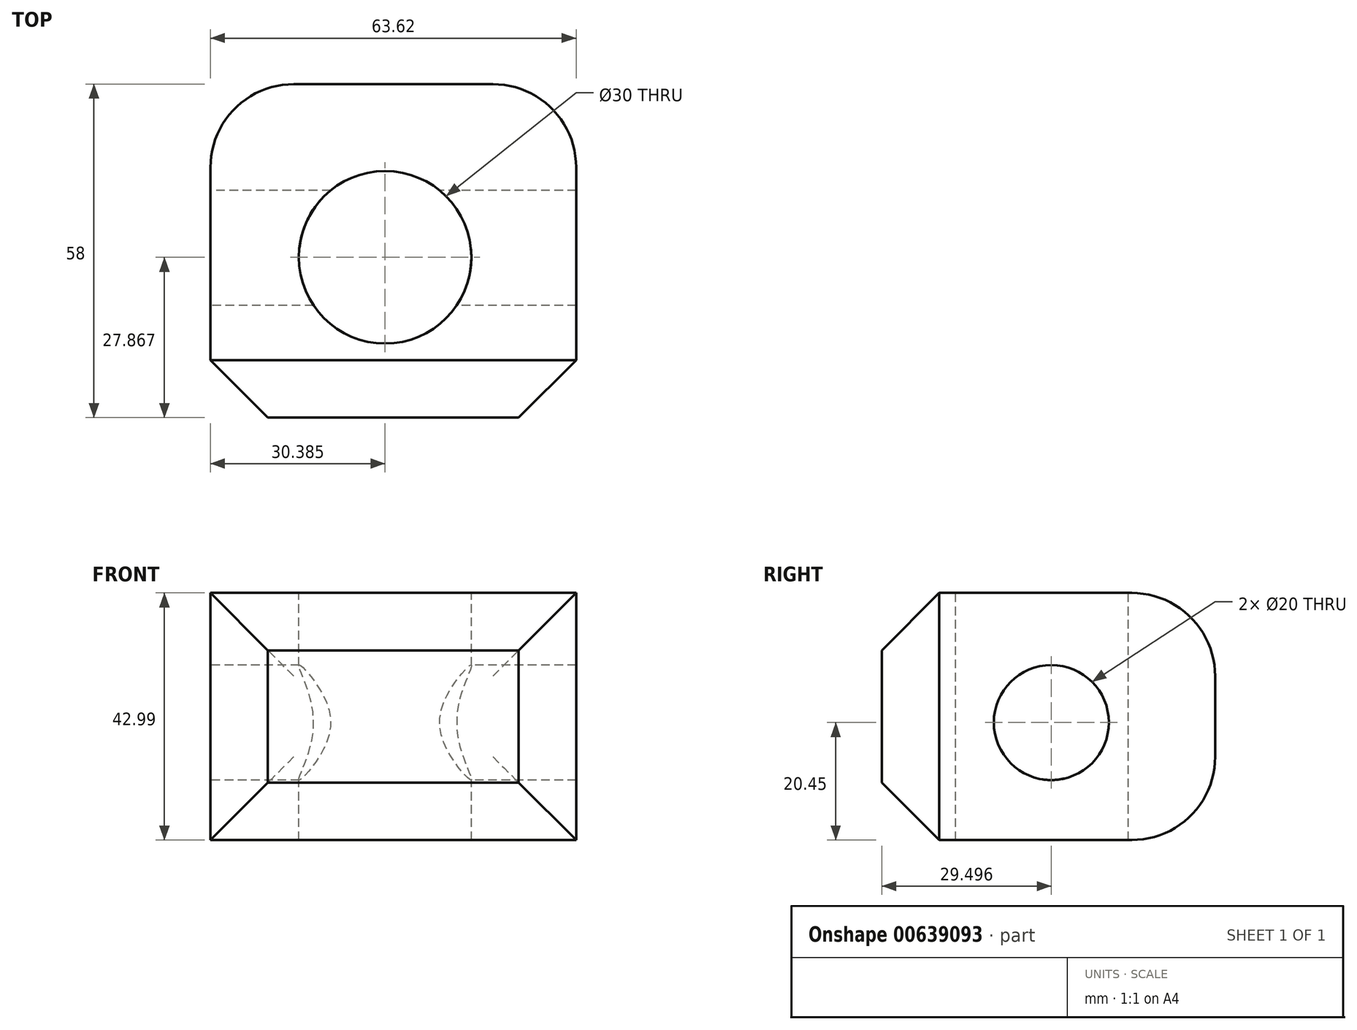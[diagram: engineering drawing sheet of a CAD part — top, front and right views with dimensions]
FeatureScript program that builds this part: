
annotation { "Feature Type Name" : "Feature", "Feature Type Description" : "" }
export const myFeature = defineFeature(function(context is Context, id is Id, definition is map)
    precondition{}
    {
        {
            var Q0;
            Q0=qCreatedBy(makeId("Front.planeOp"),FACE);
            var sketch = newSketch(context, id + "F0", { "sketchPlane" : qUnion([Q0])});
            skLineSegment(sketch, "E0.bottom", {"start": v(-27.79, 22.54) * mm, "end": v(35.83, 22.54) * mm});
            skLineSegment(sketch, "E0.top", {"start": v(-27.79, -20.45) * mm, "end": v(35.83, -20.45) * mm});
            skLineSegment(sketch, "E0.left", {"start": v(-27.79, 22.54) * mm, "end": v(-27.79, -20.45) * mm});
            skLineSegment(sketch, "E0.right", {"start": v(35.83, 22.54) * mm, "end": v(35.83, -20.45) * mm});
            skSolve(sketch);
        }
        {
            var Q0;
            Q0=makeQuery(id+"F0.imprint","IMPRINT",FACE,{"disambiguationData":[TD([[makeQuery(id+"F0.imprint","IMPRINT",EDGE,{"derivedFrom":sQuery(id+"F0.wireOp",EDGE,"E0.bottom")}),-1.0]])]});
            var sketch = newSketch(context, id + "F1", { "sketchPlane" : qUnion([Q0])});
            skSolve(sketch);
        }
        {
            var Q0;
            Q0 = qSketchRegion(id + "F1", true);
            var Q1;
            Q1=makeQuery(id+"F1.imprint","IMPRINT",FACE,{"disambiguationData":[TD([[makeQuery(id+"F1.imprint","IMPRINT",EDGE,{"derivedFrom":makeQuery(id+"F0.imprint","IMPRINT",EDGE,{"derivedFrom":sQuery(id+"F0.wireOp",EDGE,"E0.bottom")})}),-1.0]])]});
            extrude(context, id + "F2", {"entities" : qUnion([Q0, Q1]), "oppositeDirection" : true, "depth" : 58 * mm, "offsetDistance" : 25 * mm});
        }
        {
            var Q0;
            Q0=makeQuery(id+"F2.opExtrude","CAP_EDGE",EDGE,{"disambiguationData":[OSD([sQuery(id+"F0.wireOp",EDGE,"E0.left")])],"isStart":false});
            var Q1;
            Q1=makeQuery(id+"F2.opExtrude","CAP_EDGE",EDGE,{"disambiguationData":[OSD([sQuery(id+"F0.wireOp",EDGE,"E0.bottom")])],"isStart":false});
            var Q2;
            Q2=makeQuery(id+"F2.opExtrude","CAP_EDGE",EDGE,{"disambiguationData":[OSD([sQuery(id+"F0.wireOp",EDGE,"E0.right")])],"isStart":false});
            var Q3;
            Q3=makeQuery(id+"F2.opExtrude","CAP_EDGE",EDGE,{"disambiguationData":[OSD([sQuery(id+"F0.wireOp",EDGE,"E0.top")])],"isStart":false});
            fillet(context, id + "F3", {"entities" : qUnion([Q0, Q1, Q2, Q3]), "radius" : 14.5 * mm, "tangentPropagation" : true, "allowEdgeOverflow" : false});
        }
        {
            var Q0;
            Q0=makeQuery(id+"F2.opExtrude","CAP_EDGE",EDGE,{"disambiguationData":[OSD([sQuery(id+"F0.wireOp",EDGE,"E0.right")])],"isStart":true});
            var Q1;
            Q1=makeQuery(id+"F2.opExtrude","CAP_EDGE",EDGE,{"disambiguationData":[OSD([sQuery(id+"F0.wireOp",EDGE,"E0.top")])],"isStart":true});
            var Q2;
            Q2=makeQuery(id+"F2.opExtrude","CAP_EDGE",EDGE,{"disambiguationData":[OSD([sQuery(id+"F0.wireOp",EDGE,"E0.left")])],"isStart":true});
            var Q3;
            Q3=makeQuery(id+"F2.opExtrude","CAP_EDGE",EDGE,{"disambiguationData":[OSD([sQuery(id+"F0.wireOp",EDGE,"E0.bottom")])],"isStart":true});
            chamfer(context, id + "F4", {"entities" : qUnion([Q0, Q1, Q2, Q3]), "width" : 10 * mm, "tangentPropagation" : true});
        }
        {
            var Q0;
            Q0=makeQuery(id+"F2.opExtrude","SWEPT_FACE",FACE,{"disambiguationData":[OSD([sQuery(id+"F0.wireOp",EDGE,"E0.bottom")])]});
            var sketch = newSketch(context, id + "F5", { "sketchPlane" : qUnion([Q0])});
            skCircle(sketch, "E1", {"center": v(2.6, 27.87) * mm, "radius": 12.32 * mm});
            skSolve(sketch);
        }
        {
            var Q0;
            Q0=sQuery(id+"F5.wireOp",VERTEX,"E1.center");
            var Q1;
            Q1=makeQuery(id+"F2.opExtrude","SWEPT_BODY",BODY,{"disambiguationData":[OSD([sQuery(id+"F0.wireOp",EDGE,"E0.bottom"),sQuery(id+"F0.wireOp",EDGE,"E0.top"),sQuery(id+"F0.wireOp",EDGE,"E0.left"),sQuery(id+"F0.wireOp",EDGE,"E0.right")])]});
            hole(context, id + "F6", {"style" : HoleStyle.SIMPLE, "endStyle" : HoleEndStyle.THROUGH, "holeDiameter" : 30 * mm, "majorDiameter" : 5 * mm, "isTappedThrough" : true, "tappedDepth" : 12 * mm, "tapClearance" : 3, "locations" : qUnion([Q0]), "scope" : qUnion([Q1])});
        }
        {
            var Q0;
            Q0=makeQuery(id+"F2.opExtrude","SWEPT_FACE",FACE,{"disambiguationData":[OSD([sQuery(id+"F0.wireOp",EDGE,"E0.left")])]});
            var sketch = newSketch(context, id + "F7", { "sketchPlane" : qUnion([Q0])});
            skCircle(sketch, "E2", {"center": v(-29.5, 0) * mm, "radius": 10.81 * mm});
            skSolve(sketch);
        }
        {
            var Q0;
            Q0=sQuery(id+"F7.wireOp",VERTEX,"E2.center");
            var Q1;
            Q1=makeQuery(id+"F2.opExtrude","SWEPT_BODY",BODY,{"disambiguationData":[OSD([sQuery(id+"F0.wireOp",EDGE,"E0.bottom"),sQuery(id+"F0.wireOp",EDGE,"E0.top"),sQuery(id+"F0.wireOp",EDGE,"E0.left"),sQuery(id+"F0.wireOp",EDGE,"E0.right")])]});
            hole(context, id + "F8", {"style" : HoleStyle.SIMPLE, "endStyle" : HoleEndStyle.THROUGH, "holeDiameter" : 20 * mm, "majorDiameter" : 5 * mm, "isTappedThrough" : true, "tappedDepth" : 12 * mm, "tapClearance" : 3, "locations" : qUnion([Q0]), "scope" : qUnion([Q1])});
        }
    });
